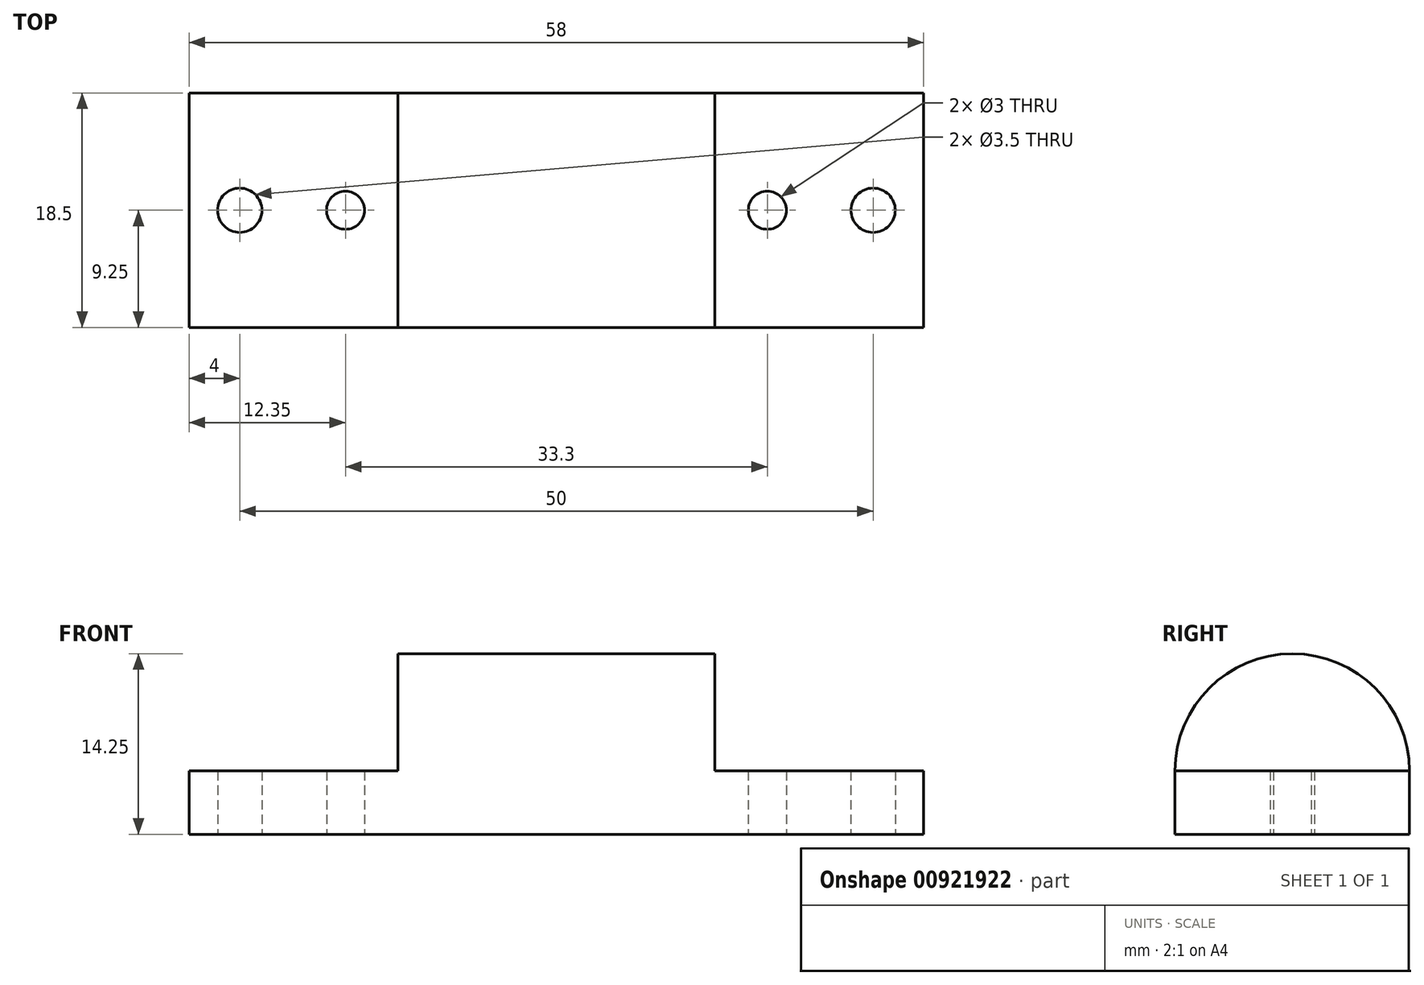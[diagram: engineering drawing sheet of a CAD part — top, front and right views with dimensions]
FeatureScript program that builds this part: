
annotation { "Feature Type Name" : "Feature", "Feature Type Description" : "" }
export const myFeature = defineFeature(function(context is Context, id is Id, definition is map)
    precondition{}
    {
        {
            var Q0;
            Q0=qCreatedBy(makeId("Top.planeOp"),FACE);
            var sketch = newSketch(context, id + "F0", { "sketchPlane" : qUnion([Q0])});
            skLineSegment(sketch, "E0.bottom", {"start": v(19, -9.25) * mm, "end": v(-19, -9.25) * mm});
            skLineSegment(sketch, "E0.top", {"start": v(19, 9.25) * mm, "end": v(-19, 9.25) * mm});
            skLineSegment(sketch, "E0.left", {"start": v(19, -9.25) * mm, "end": v(19, 9.25) * mm});
            skLineSegment(sketch, "E0.right", {"start": v(-19, -9.25) * mm, "end": v(-19, 9.25) * mm});
            skPoint(sketch, "E0.middle", {"position": v(0, 0) * mm});
            skLineSegment(sketch, "E1.bottom", {"start": v(19, -9.25) * mm, "end": v(29, -9.25) * mm});
            skLineSegment(sketch, "E1.top", {"start": v(19, 9.25) * mm, "end": v(29, 9.25) * mm});
            skLineSegment(sketch, "E1.right", {"start": v(29, -9.25) * mm, "end": v(29, 9.25) * mm});
            skLineSegment(sketch, "E2.bottom", {"start": v(-19, -9.25) * mm, "end": v(-29, -9.25) * mm});
            skLineSegment(sketch, "E2.top", {"start": v(-19, 9.25) * mm, "end": v(-29, 9.25) * mm});
            skLineSegment(sketch, "E2.right", {"start": v(-29, -9.25) * mm, "end": v(-29, 9.25) * mm});
            skCircle(sketch, "E3", {"center": v(-25, 0) * mm, "radius": 1.75 * mm});
            skPoint(sketch, "E3.centerSnap0", {"position": v(-29, 0) * mm});
            skCircle(sketch, "E4", {"center": v(25, 0) * mm, "radius": 1.75 * mm});
            skPoint(sketch, "E4.centerSnap0", {"position": v(29, 0) * mm});
            skCircle(sketch, "E5", {"center": v(-16.65, 0) * mm, "radius": 1.5 * mm});
            skCircle(sketch, "E6", {"center": v(16.65, 0) * mm, "radius": 1.5 * mm});
            skSolve(sketch);
        }
        {
            var Q0;
            Q0=qSketchRegion(id+"F0",true);
            extrude(context, id + "F1", {"entities" : qUnion([Q0]), "depth" : 5 * mm, "offsetDistance" : 25 * mm});
        }
        {
            var Q0;
            Q0=makeQuery(id+"F1.opExtrude","CAP_FACE",FACE,{"disambiguationData":[OSD([sQuery(id+"F0.wireOp",EDGE,"E0.bottom"),sQuery(id+"F0.wireOp",EDGE,"E0.top"),sQuery(id+"F0.wireOp",EDGE,"E1.bottom"),sQuery(id+"F0.wireOp",EDGE,"E1.top"),sQuery(id+"F0.wireOp",EDGE,"E1.right"),sQuery(id+"F0.wireOp",EDGE,"E2.bottom"),sQuery(id+"F0.wireOp",EDGE,"E2.top"),sQuery(id+"F0.wireOp",EDGE,"E2.right"),sQuery(id+"F0.wireOp",EDGE,"E3"),sQuery(id+"F0.wireOp",EDGE,"E4"),sQuery(id+"F0.wireOp",EDGE,"E5"),sQuery(id+"F0.wireOp",EDGE,"E6")])],"isStart":false});
            var sketch = newSketch(context, id + "F2", { "sketchPlane" : qUnion([Q0])});
            skLineSegment(sketch, "E7.bottom", {"start": v(12.5, -9.25) * mm, "end": v(-12.5, -9.25) * mm});
            skLineSegment(sketch, "E7.top", {"start": v(12.5, 9.25) * mm, "end": v(-12.5, 9.25) * mm});
            skLineSegment(sketch, "E7.left", {"start": v(12.5, -9.25) * mm, "end": v(12.5, 9.25) * mm});
            skLineSegment(sketch, "E7.right", {"start": v(-12.5, -9.25) * mm, "end": v(-12.5, 9.25) * mm});
            skPoint(sketch, "E7.middle", {"position": v(0, 0) * mm});
            skSolve(sketch);
        }
        {
            var Q0;
            Q0 = qSketchRegion(id + "F2", true);
            extrude(context, id + "F3", {"entities" : qUnion([Q0]), "operationType" : NewBodyOperationType.ADD, "depth" : 18.5 / 2 * mm, "offsetDistance" : 25 * mm});
        }
        {
            var Q0;
            Q0=makeQuery(id+"F3.opExtrude","SWEPT_FACE",FACE,{"disambiguationData":[OSD([sQuery(id+"F2.wireOp",EDGE,"E7.right")])]});
            var sketch = newSketch(context, id + "F4", { "sketchPlane" : qUnion([Q0])});
            skArc(sketch, "E8", {"start": v(9.25, 5) * mm, "mid": v(0, 14.25) * mm, "end": v(-9.25, 5) * mm});
            skSolve(sketch);
        }
        {
            var Q0;
            Q0 = qSketchRegion(id + "F4", true);
            var Q1;
            {var subQ1=sQuery(id+"F2.wireOp",EDGE,"E7.right");var subQ2=makeQuery(id+"F3.opExtrude","SWEPT_EDGE",EDGE,{"disambiguationData":[OSD([sQuery(id+"F0.wireOp",EDGE,"E0.top"),sQuery(id+"F0.wireOp",EDGE,"E1.top"),sQuery(id+"F0.wireOp",EDGE,"E2.top"),sQuery(id+"F2.wireOp",EDGE,"E7.top"),subQ1])]});Q1=makeQuery(id+"F4.imprint","IMPRINT",FACE,{"disambiguationData":[TD([[makeQuery(id+"F4.imprint","IMPRINT",EDGE,{"derivedFrom":subQ2}),1.0]])]});}
            var Q2;
            {var subQ1=sQuery(id+"F2.wireOp",EDGE,"E7.right");var subQ2=makeQuery(id+"F3.opExtrude","SWEPT_EDGE",EDGE,{"disambiguationData":[OSD([sQuery(id+"F0.wireOp",EDGE,"E0.bottom"),sQuery(id+"F0.wireOp",EDGE,"E1.bottom"),sQuery(id+"F0.wireOp",EDGE,"E2.bottom"),sQuery(id+"F2.wireOp",EDGE,"E7.bottom"),subQ1])]});Q2=makeQuery(id+"F4.imprint","IMPRINT",FACE,{"disambiguationData":[TD([[makeQuery(id+"F4.imprint","IMPRINT",EDGE,{"derivedFrom":subQ2}),-1.0]])]});}
            extrude(context, id + "F5", {"entities" : qUnion([Q0, Q1, Q2]), "operationType" : NewBodyOperationType.REMOVE, "oppositeDirection" : true, "depth" : 25 * mm, "offsetDistance" : 25 * mm});
        }
    });
